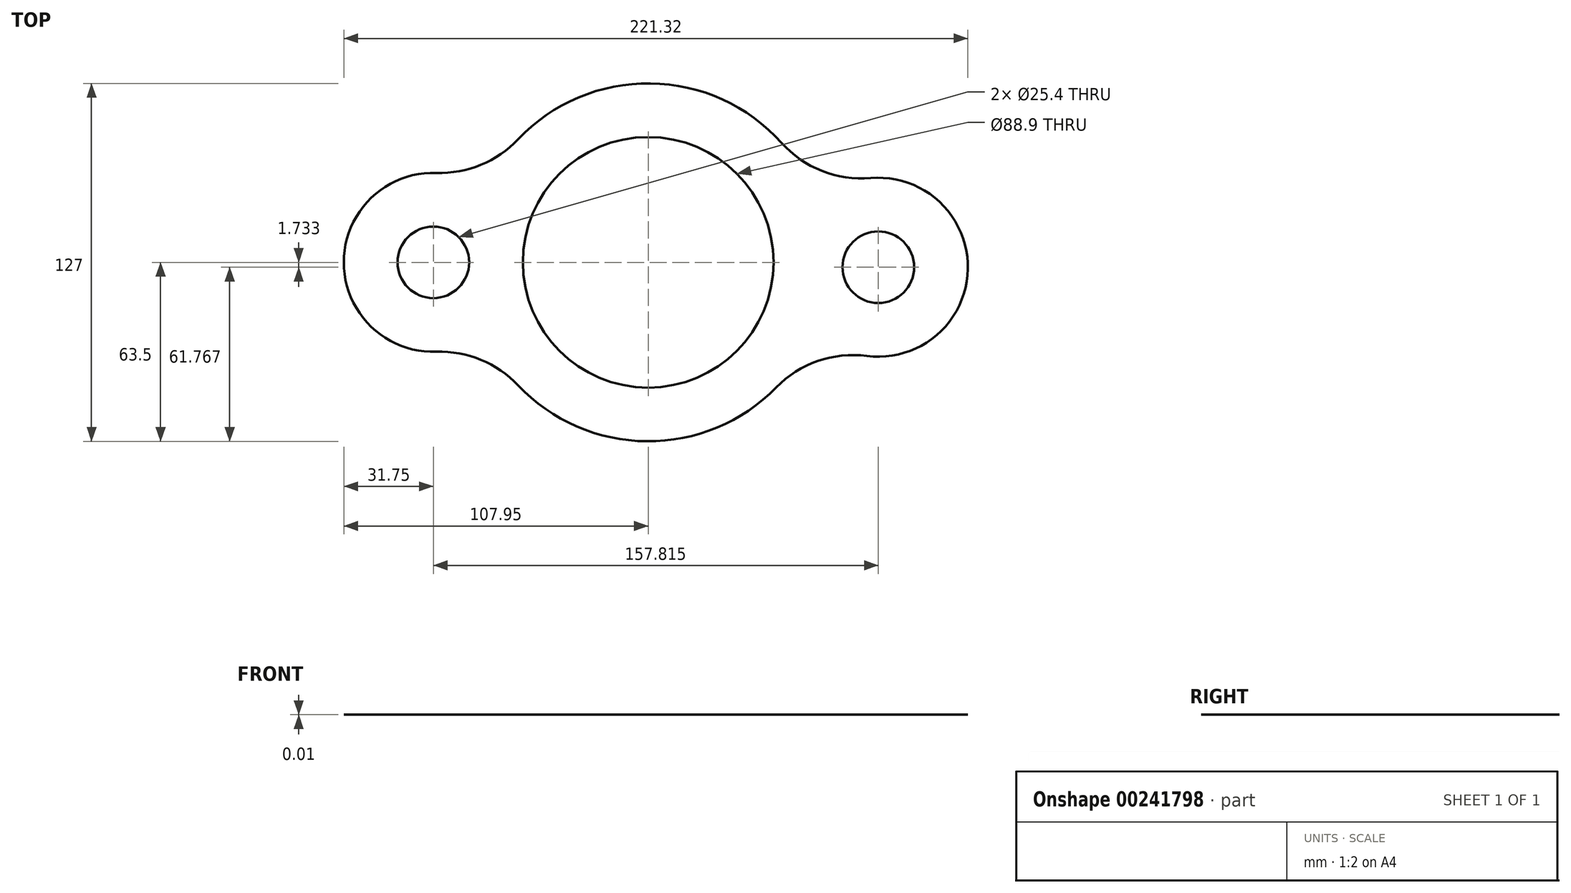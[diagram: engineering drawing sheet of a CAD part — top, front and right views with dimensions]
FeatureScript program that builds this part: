
annotation { "Feature Type Name" : "Feature", "Feature Type Description" : "" }
export const myFeature = defineFeature(function(context is Context, id is Id, definition is map)
    precondition{}
    {
        {
            var Q0;
            Q0=qCreatedBy(makeId("Top.planeOp"),FACE);
            var sketch = newSketch(context, id + "F0", { "sketchPlane" : qUnion([Q0])});
            skCircle(sketch, "E0", {"center": v(0, 0) * mm, "radius": 44.45 * mm});
            skLineSegment(sketch, "E1", {"start": v(0, 0) * mm, "end": v(-76.2, 0) * mm, "construction": true});
            skLineSegment(sketch, "E2", {"start": v(0, 0) * mm, "end": v(76.2, 0) * mm, "construction": true});
            skCircle(sketch, "E3", {"center": v(-76.2, 0) * mm, "radius": 12.7 * mm});
            skCircle(sketch, "E4", {"center": v(81.62, -1.73) * mm, "radius": 12.7 * mm});
            skArc(sketch, "E5", {"start": v(-75.12, 31.73) * mm, "mid": v(-107.95, 0) * mm, "end": v(-75.12, -31.73) * mm});
            skArc(sketch, "E6", {"start": v(77.55, -33.22) * mm, "mid": v(113.36, -2.4) * mm, "end": v(78.89, 29.9) * mm});
            skArc(sketch, "E7", {"start": v(-46.14, -43.63) * mm, "mid": v(-0.52, -63.5) * mm, "end": v(45.42, -44.38) * mm});
            skArc(sketch, "E8.trimOffspring", {"start": v(47.26, 42.41) * mm, "mid": v(0.83, 63.5) * mm, "end": v(-46.14, 43.63) * mm});
            skPoint(sketch, "E9.visualSharp", {"position": v(59.8, 21.34) * mm});
            skArc(sketch, "E9.filletArc", {"start": v(47.26, 42.41) * mm, "mid": v(61.6, 32.43) * mm, "end": v(78.89, 29.9) * mm});
            skPoint(sketch, "E10.visualSharp", {"position": v(58.85, -23.86) * mm});
            skArc(sketch, "E10.filletArc", {"start": v(77.55, -33.22) * mm, "mid": v(60.17, -35.02) * mm, "end": v(45.42, -44.38) * mm});
            skPoint(sketch, "E11.visualSharp", {"position": v(-57.94, 25.98) * mm});
            skArc(sketch, "E11.filletArc", {"start": v(-75.12, 31.73) * mm, "mid": v(-59.35, 34.56) * mm, "end": v(-46.14, 43.63) * mm});
            skPoint(sketch, "E12.visualSharp", {"position": v(-57.94, -25.98) * mm});
            skArc(sketch, "E12.filletArc", {"start": v(-46.14, -43.63) * mm, "mid": v(-59.35, -34.56) * mm, "end": v(-75.12, -31.73) * mm});
            skSolve(sketch);
        }
        {
            var Q0;
            Q0=makeQuery(id+"F0.imprint","IMPRINT",FACE,{"disambiguationData":[TD([[makeQuery(id+"F0.imprint","IMPRINT",EDGE,{"derivedFrom":sQuery(id+"F0.wireOp",EDGE,"E0")}),-1.0]])]});
            extrude(context, id + "F1", {"entities" : qUnion([Q0]), "depth" : 1 / 101.6 * mm});
        }
    });
